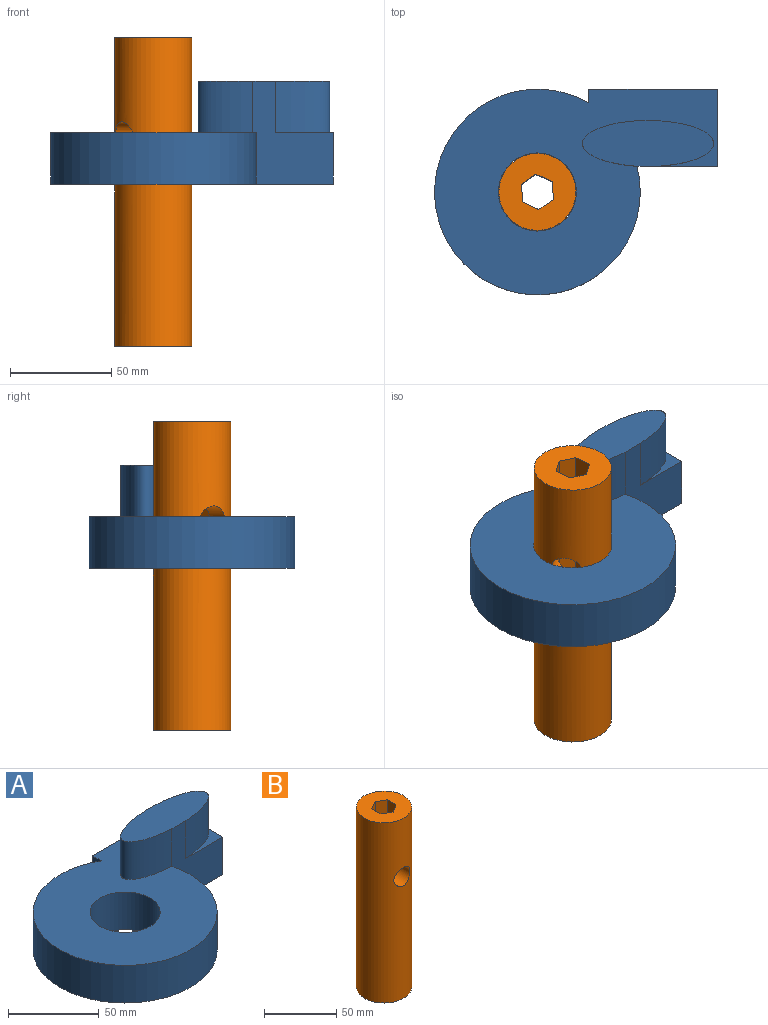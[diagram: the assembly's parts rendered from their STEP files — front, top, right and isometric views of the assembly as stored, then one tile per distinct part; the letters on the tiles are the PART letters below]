
ASSEMBLY  parts=2 mates=1
PART A: 10 faces, bbox 139.7x101.6x50.8 mm
  f0: plane 63.5x25.4mm, normal (0,1,0), area 1612.9mm2, adj f1,f4,f5,f6
  f1: plane 25.4x6.81mm, normal (-1,0,0), area 172.9mm2, adj f0,f2,f5,f6
  f2: cylinder r=50.8mm len=101.6mm, axis (0,0,-1), area 7082.1mm2, adj f1,f3,f5,f6
  f3: plane 50.8x39.71mm, normal (0,-1,0), area 1286mm2, adj f2,f4,f5,f6,f8,f9
  f4: plane 38.1x25.4mm, normal (1,0,0), area 967.7mm2, adj f0,f3,f5,f6
  f5: plane 139.7x101.6mm, normal (0,0,1), area 7718.9mm2, adj f0,f1,f2,f3,f4,f7,f8
  f6: plane 139.7x101.6mm, normal (0,0,-1), area 8879.3mm2, adj f0,f1,f2,f3,f4,f7
  f7: cylinder r=19.3mm len=38.61mm, axis (0,0,1), area 3080.8mm2, adj f5,f6
  f8: extruded ~64.63x25.4mm, area 3424.8mm2, adj f3,f5,f9
  f9: plane 64.86x22.64mm, normal (0,0,1), area 1160.4mm2, adj f3,f8
PART B: 16 faces, bbox 38.1x38.1x152.4 mm
  f0: plane 47.85x7.62mm, normal (0.5,-0.87,0), area 379.8mm2, adj f7,f11,f13,f15
  f1: plane 101.51x7.62mm, normal (-0.5,-0.87,0), area 852mm2, adj f6,f8,f14,f15
  f2: plane 47.85x8.8mm, normal (-1,0,0), area 421mm2, adj f7,f9,f13,f15
  f3: plane 101.51x7.62mm, normal (-0.5,0.87,0), area 852mm2, adj f8,f10,f14,f15
  f4: plane 47.85x7.62mm, normal (0.5,0.87,0), area 379.8mm2, adj f9,f11,f13,f15
  f5: plane 101.51x8.8mm, normal (1,0,0), area 893.2mm2, adj f6,f10,f14,f15
  f6: plane 101.51x7.62mm, normal (0.5,-0.87,0), area 852mm2, adj f1,f5,f14,f15
  f7: plane 47.85x7.62mm, normal (-0.5,-0.87,0), area 379.8mm2, adj f0,f2,f13,f15
  f8: plane 101.51x8.8mm, normal (-1,0,0), area 893.2mm2, adj f1,f3,f14,f15
  f9: plane 47.85x7.62mm, normal (-0.5,0.87,0), area 379.8mm2, adj f2,f4,f13,f15
  f10: plane 101.51x7.62mm, normal (0.5,0.87,0), area 852mm2, adj f3,f5,f14,f15
  f11: plane 47.85x8.8mm, normal (1,0,0), area 421mm2, adj f0,f4,f13,f15
  f12: cylinder r=19.05mm len=152.4mm, axis (0,0,-1), area 17854.3mm2, adj f13,f14,f15
  f13: plane 38.1x38.1mm, normal (0,0,1), area 939mm2, adj f0,f2,f4,f7,f9,f11,f12
  f14: plane 38.1x38.1mm, normal (0,0,-1), area 939mm2, adj f1,f3,f5,f6,f8,f10,f12
  f15: cylinder r=7.77mm len=38.1mm, axis (0,-1,0), area 1252.8mm2, adj f0,f1,f2,f3,f4,f5,f6,f7
PLACE A t=(16.25,13.96,-21.49)mm fixed
PLACE B rot(axis=(0,0,1),124.6deg) t=(16.25,13.96,-101.61)mm
MATE cylindrical B.f12 <-> A.f2  axis (0,0,-1) through (16.25,13.96,-25.41)mm
